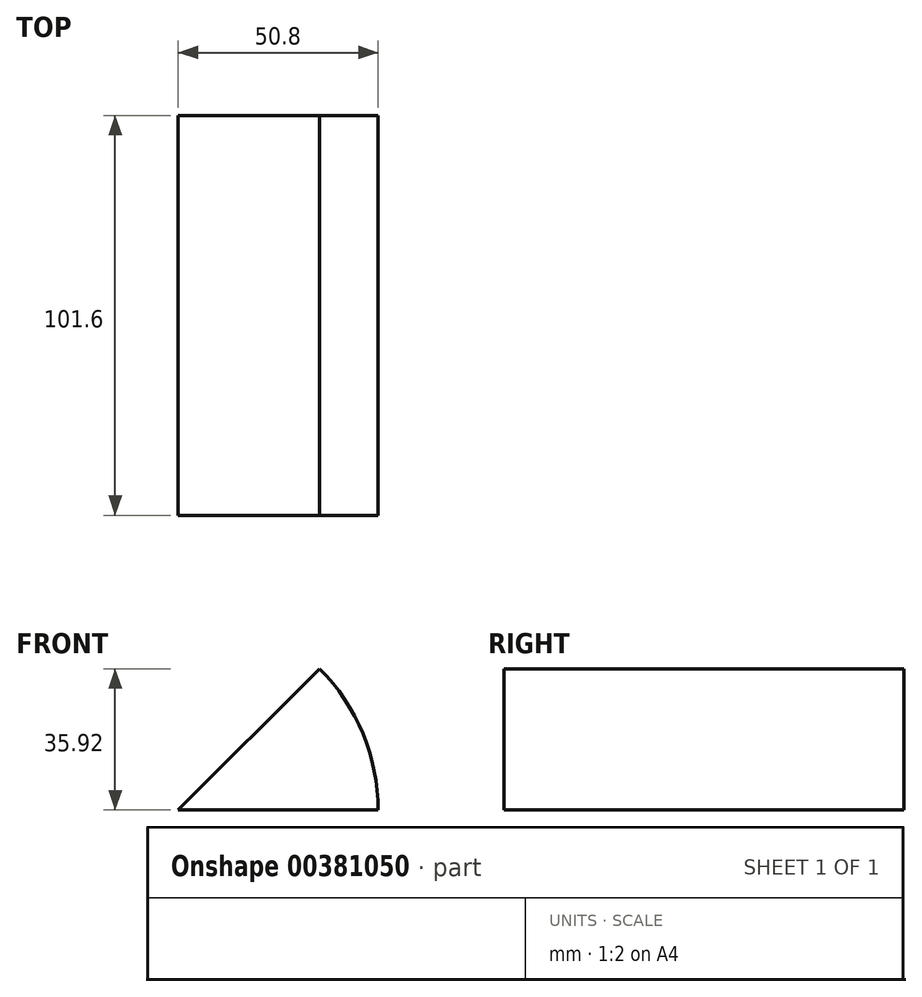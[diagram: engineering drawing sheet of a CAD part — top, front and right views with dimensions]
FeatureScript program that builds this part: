
annotation { "Feature Type Name" : "Feature", "Feature Type Description" : "" }
export const myFeature = defineFeature(function(context is Context, id is Id, definition is map)
    precondition{}
    {
        {
            var Q0;
            Q0=qCreatedBy(makeId("Front.planeOp"),FACE);
            var sketch = newSketch(context, id + "F0", { "sketchPlane" : qUnion([Q0])});
            skArc(sketch, "E0", {"start": v(50.8, 0) * mm, "mid": v(46.93, 19.44) * mm, "end": v(35.92, 35.92) * mm});
            skLineSegment(sketch, "E1", {"start": v(50.8, 0) * mm, "end": v(0, 0) * mm});
            skLineSegment(sketch, "E2", {"start": v(0, 0) * mm, "end": v(35.92, 35.92) * mm});
            skSolve(sketch);
        }
        {
            var Q0;
            Q0=makeQuery(id+"F0.imprint","IMPRINT",FACE,{"disambiguationData":[TD([[makeQuery(id+"F0.imprint","IMPRINT",EDGE,{"derivedFrom":sQuery(id+"F0.wireOp",EDGE,"E0")}),1.0]])]});
            extrude(context, id + "F1", {"entities" : qUnion([Q0]), "depth" : 101.6 * mm});
        }
    });
